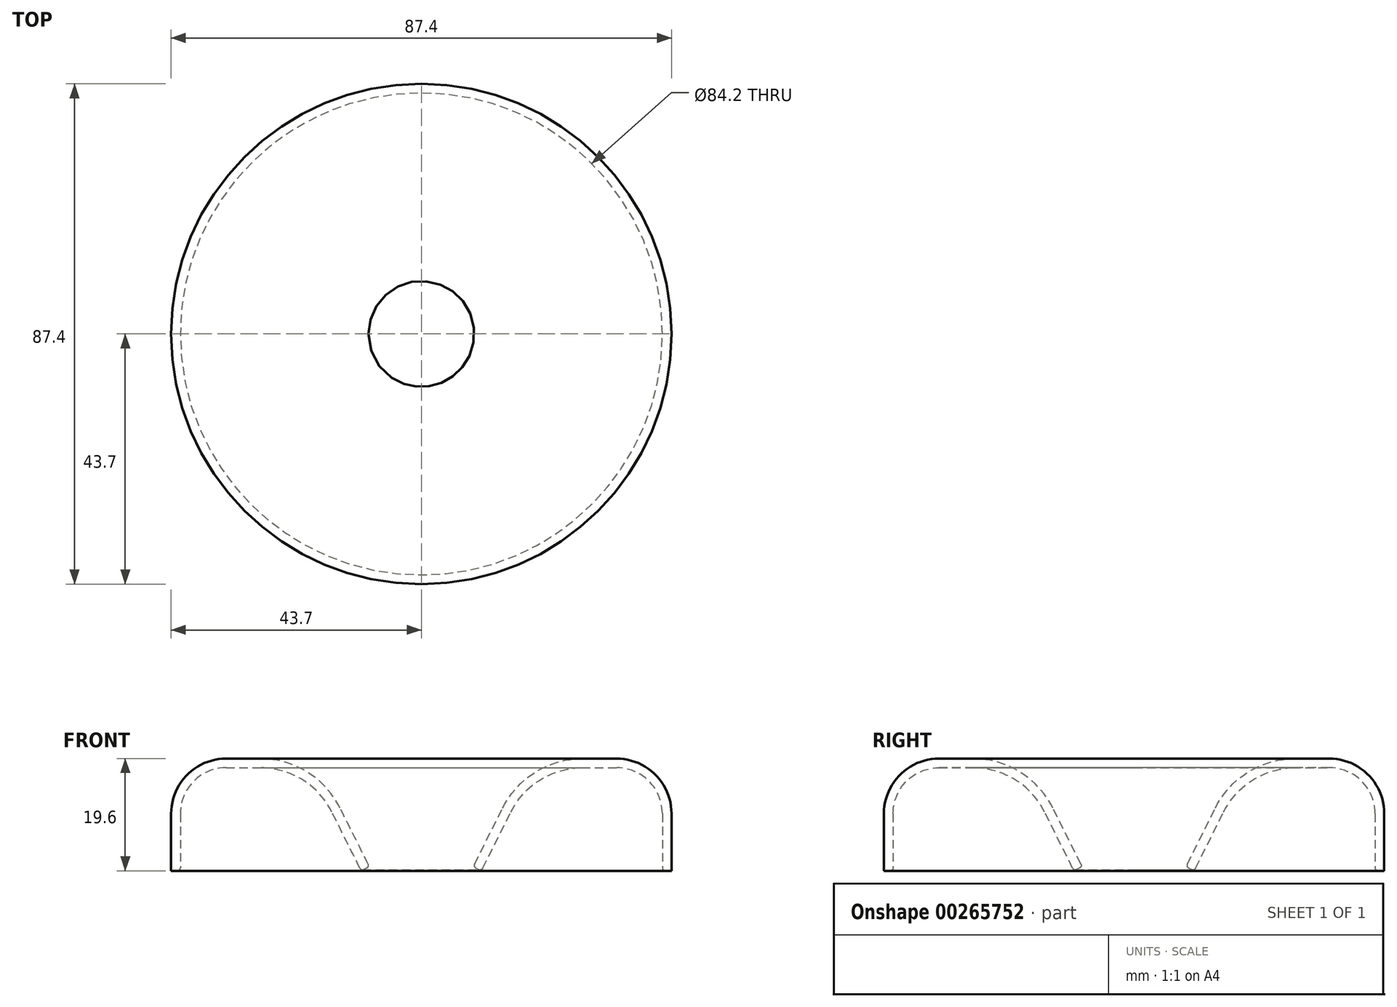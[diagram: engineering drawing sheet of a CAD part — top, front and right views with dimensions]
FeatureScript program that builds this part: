
annotation { "Feature Type Name" : "Feature", "Feature Type Description" : "" }
export const myFeature = defineFeature(function(context is Context, id is Id, definition is map)
    precondition{}
    {
        {
            var Q0;
            Q0=qCreatedBy(makeId("Front.planeOp"),FACE);
            var sketch = newSketch(context, id + "F0", { "sketchPlane" : qUnion([Q0])});
            skLineSegment(sketch, "E0", {"start": v(-10.72, 0.45) * mm, "end": v(-15.63, 10.26) * mm});
            skLineSegment(sketch, "E1", {"start": v(-28.15, 18) * mm, "end": v(-34.1, 18) * mm});
            skLineSegment(sketch, "E2", {"start": v(-42.1, 10) * mm, "end": v(-42.1, 0.5) * mm});
            skPoint(sketch, "E3.visualSharp", {"position": v(-42.1, 18) * mm});
            skArc(sketch, "E3.filletArc", {"start": v(-34.1, 18) * mm, "mid": v(-39.76, 15.66) * mm, "end": v(-42.1, 10) * mm});
            skPoint(sketch, "E4.visualSharp", {"position": v(-19.5, 18) * mm});
            skArc(sketch, "E4.filletArc", {"start": v(-15.63, 10.26) * mm, "mid": v(-20.8, 15.9) * mm, "end": v(-28.15, 18) * mm});
            skLineSegment(sketch, "E5.0", {"start": v(-43.7, 10) * mm, "end": v(-43.7, 0) * mm});
            skLineSegment(sketch, "E5.1", {"start": v(-9.3, 1.16) * mm, "end": v(-14.2, 10.98) * mm});
            skArc(sketch, "E5.2", {"start": v(-14.2, 10.98) * mm, "mid": v(-19.95, 17.27) * mm, "end": v(-28.15, 19.6) * mm});
            skLineSegment(sketch, "E5.3", {"start": v(-28.15, 19.6) * mm, "end": v(-34.1, 19.6) * mm});
            skArc(sketch, "E5.4", {"start": v(-34.1, 19.6) * mm, "mid": v(-40.89, 16.79) * mm, "end": v(-43.7, 10) * mm});
            skLineSegment(sketch, "E6", {"start": v(-10.05, 0.22) * mm, "end": v(-9.52, 0.5) * mm});
            skLineSegment(sketch, "E7", {"start": v(-43.7, 0) * mm, "end": v(-42.6, 0) * mm});
            skPoint(sketch, "E8.visualSharp", {"position": v(-9.07, 0.72) * mm});
            skArc(sketch, "E8.filletArc", {"start": v(-9.52, 0.5) * mm, "mid": v(-9.27, 0.78) * mm, "end": v(-9.3, 1.16) * mm});
            skPoint(sketch, "E9.visualSharp", {"position": v(-10.5, 0) * mm});
            skArc(sketch, "E9.filletArc", {"start": v(-10.72, 0.45) * mm, "mid": v(-10.43, 0.2) * mm, "end": v(-10.05, 0.22) * mm});
            skPoint(sketch, "E10.visualSharp", {"position": v(-42.1, 0) * mm});
            skArc(sketch, "E10.filletArc", {"start": v(-42.6, 0) * mm, "mid": v(-42.25, 0.15) * mm, "end": v(-42.1, 0.5) * mm});
            skLineSegment(sketch, "E11", {"start": v(0, 0) * mm, "end": v(0, 1.47) * mm});
            skSolve(sketch);
        }
        {
            var Q0;
            Q0=makeQuery(id+"F0.imprint","IMPRINT",FACE,{"disambiguationData":[TD([[makeQuery(id+"F0.imprint","IMPRINT",EDGE,{"derivedFrom":sQuery(id+"F0.wireOp",EDGE,"E0")}),-1.0]])]});
            var Q1;
            Q1=sQuery(id+"F0.wireOp",EDGE,"E11");
            revolve(context, id + "F1", {"entities" : qUnion([Q0]), "axis" : qUnion([Q1]), "revolveType" : RevolveType.FULL});
        }
    });
